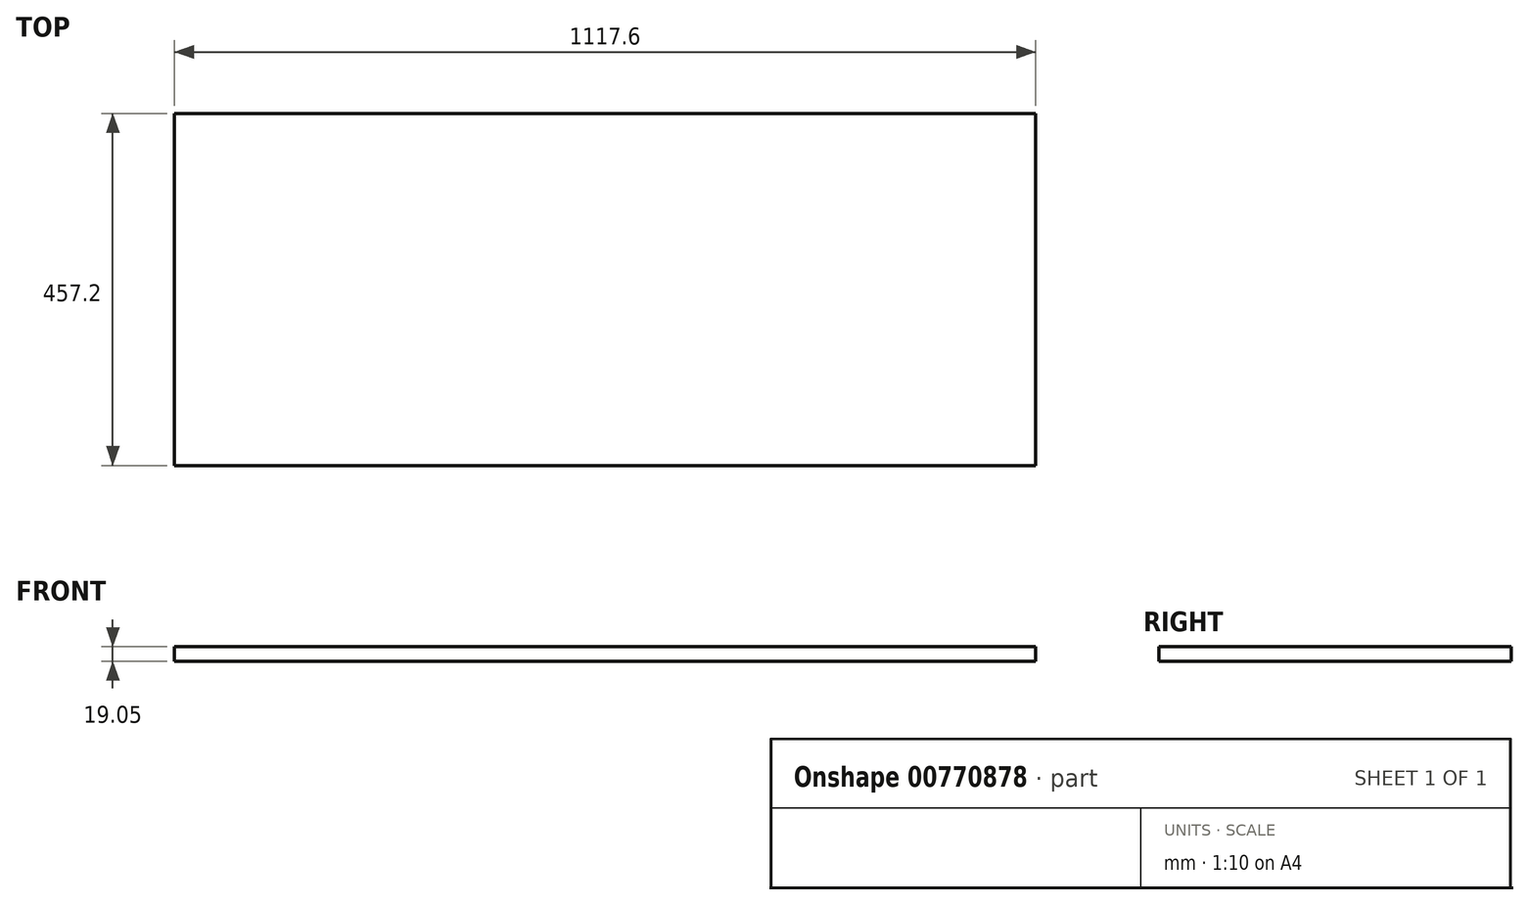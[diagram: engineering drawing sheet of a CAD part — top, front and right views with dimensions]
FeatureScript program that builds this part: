
annotation { "Feature Type Name" : "Feature", "Feature Type Description" : "" }
export const myFeature = defineFeature(function(context is Context, id is Id, definition is map)
    precondition{}
    {
        {
            var Q0;
            Q0=qCreatedBy(makeId("Top.planeOp"),FACE);
            var sketch = newSketch(context, id + "F0", { "sketchPlane" : qUnion([Q0])});
            skLineSegment(sketch, "E0.bottom", {"start": v(567.7, 228.6) * mm, "end": v(-549.9, 228.6) * mm});
            skLineSegment(sketch, "E0.top", {"start": v(567.7, -228.6) * mm, "end": v(-549.9, -228.6) * mm});
            skLineSegment(sketch, "E0.left", {"start": v(567.7, 228.6) * mm, "end": v(567.7, -228.6) * mm});
            skLineSegment(sketch, "E0.right", {"start": v(-549.9, 228.6) * mm, "end": v(-549.9, -228.6) * mm});
            skPoint(sketch, "E0.middle", {"position": v(8.9, 0) * mm});
            skSolve(sketch);
        }
        {
            var Q0;
            Q0=qSketchRegion(id+"F0",true);
            extrude(context, id + "F1", {"entities" : qUnion([Q0]), "depth" : 19.05 * mm, "offsetDistance" : 25.4 * mm});
        }
    });
